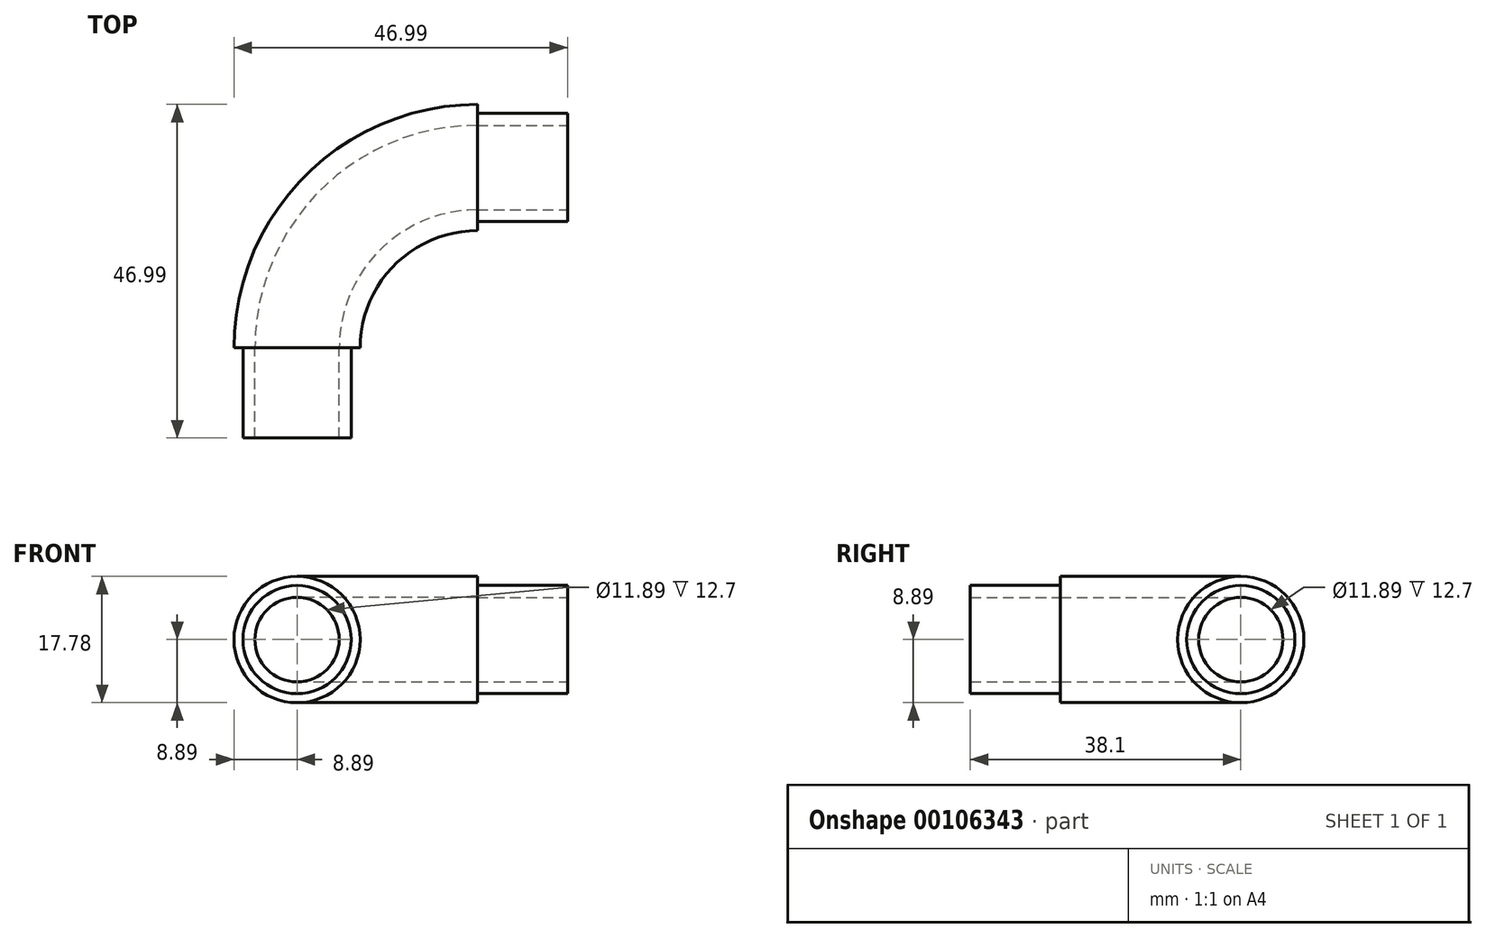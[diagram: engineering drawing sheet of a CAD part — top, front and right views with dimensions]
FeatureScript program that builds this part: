
annotation { "Feature Type Name" : "Feature", "Feature Type Description" : "" }
export const myFeature = defineFeature(function(context is Context, id is Id, definition is map)
    precondition{}
    {
        {
            var Q0;
            Q0=qCreatedBy(makeId("Front.planeOp"),FACE);
            var sketch = newSketch(context, id + "F0", { "sketchPlane" : qUnion([Q0])});
            skCircle(sketch, "E0", {"center": v(0, 0) * mm, "radius": 8.9 * mm});
            skCircle(sketch, "E1", {"center": v(0, 0) * mm, "radius": 5.94 * mm});
            skSolve(sketch);
        }
        {
            var Q0;
            Q0=qCreatedBy(makeId("Top.planeOp"),FACE);
            var sketch = newSketch(context, id + "F1", { "sketchPlane" : qUnion([Q0])});
            skLineSegment(sketch, "E2", {"start": v(0, 0) * mm, "end": v(0, 12.7) * mm});
            skArc(sketch, "E3", {"start": v(0, 12.7) * mm, "mid": v(7.44, 30.66) * mm, "end": v(25.4, 38.1) * mm});
            skLineSegment(sketch, "E4", {"start": v(25.4, 38.1) * mm, "end": v(38.1, 38.1) * mm});
            skSolve(sketch);
        }
        {
            var Q0;
            Q0=makeQuery(id+"F0.imprint","IMPRINT",FACE,{"disambiguationData":[TD([[makeQuery(id+"F0.imprint","IMPRINT",EDGE,{"derivedFrom":sQuery(id+"F0.wireOp",EDGE,"E0")}),1.0]])]});
            var Q1;
            Q1=sQuery(id+"F1.wireOp",EDGE,"E2");
            var Q2;
            Q2=sQuery(id+"F1.wireOp",EDGE,"E3");
            var Q3;
            Q3=sQuery(id+"F1.wireOp",EDGE,"E4");
            sweep(context, id + "F2", {"profiles" : qUnion([Q0]), "path" : qUnion([Q1, Q2, Q3])});
        }
        {
            var Q0;
            Q0=makeQuery(id+"F2.opSweep","CAP_FACE",FACE,{"disambiguationData":[OSD([sQuery(id+"F0.wireOp",EDGE,"E0"),sQuery(id+"F0.wireOp",EDGE,"E1"),sQuery(id+"F1.wireOp",VERTEX,"E2.start")])],"isStart":true});
            var sketch = newSketch(context, id + "F3", { "sketchPlane" : qUnion([Q0])});
            skCircle(sketch, "E5", {"center": v(0, 0) * mm, "radius": 7.62 * mm});
            skSolve(sketch);
        }
        {
            var Q0;
            Q0=makeQuery(id+"F3.imprint","IMPRINT",FACE,{"disambiguationData":[TD([[makeQuery(id+"F3.imprint","IMPRINT",EDGE,{"derivedFrom":sQuery(id+"F3.wireOp",EDGE,"E5")}),-1.0]])]});
            extrude(context, id + "F4", {"entities" : qUnion([Q0]), "operationType" : NewBodyOperationType.REMOVE, "oppositeDirection" : true, "depth" : 12.7 * mm});
        }
        {
            var Q0;
            Q0=makeQuery(id+"F2.opSweep","CAP_FACE",FACE,{"disambiguationData":[OSD([sQuery(id+"F0.wireOp",EDGE,"E0"),sQuery(id+"F0.wireOp",EDGE,"E1"),sQuery(id+"F1.wireOp",VERTEX,"E4.end")])],"isStart":false});
            var sketch = newSketch(context, id + "F5", { "sketchPlane" : qUnion([Q0])});
            skCircle(sketch, "E6", {"center": v(38.1, 0) * mm, "radius": 7.62 * mm});
            skSolve(sketch);
        }
        {
            var Q0;
            Q0=makeQuery(id+"F5.imprint","IMPRINT",FACE,{"disambiguationData":[TD([[makeQuery(id+"F5.imprint","IMPRINT",EDGE,{"derivedFrom":sQuery(id+"F5.wireOp",EDGE,"E6")}),-1.0]])]});
            extrude(context, id + "F6", {"entities" : qUnion([Q0]), "operationType" : NewBodyOperationType.REMOVE, "oppositeDirection" : true, "depth" : 12.7 * mm});
        }
    });
